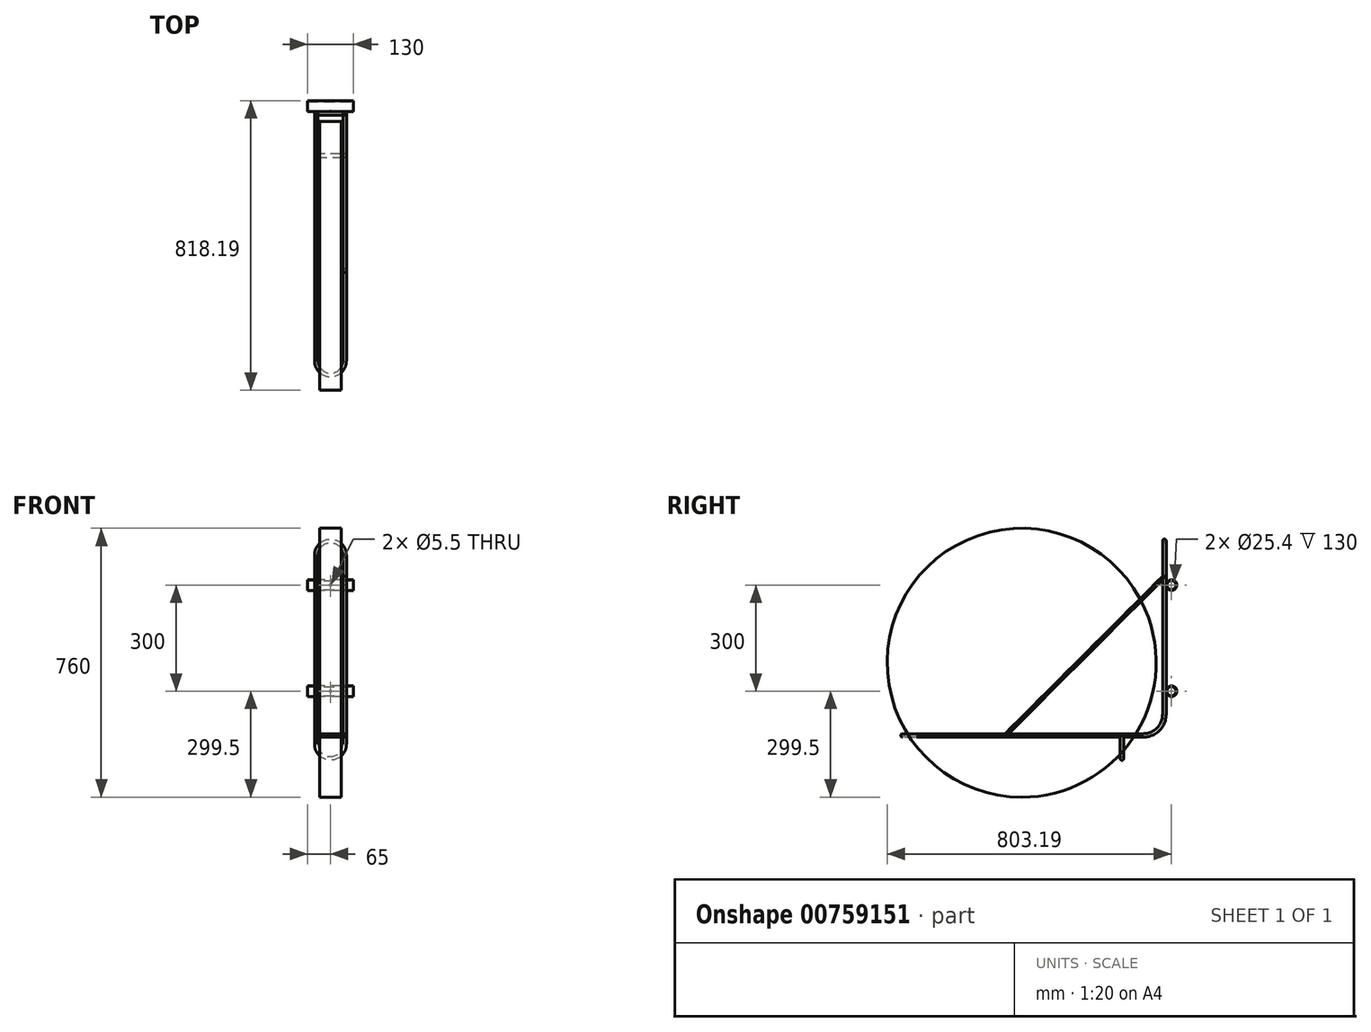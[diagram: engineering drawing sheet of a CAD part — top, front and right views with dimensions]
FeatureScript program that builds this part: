
annotation { "Feature Type Name" : "Feature", "Feature Type Description" : "" }
export const myFeature = defineFeature(function(context is Context, id is Id, definition is map)
    precondition{}
    {
        {
            var Q0;
            Q0=qCreatedBy(makeId("Right.planeOp"),FACE);
            var sketch = newSketch(context, id + "F0", { "sketchPlane" : qUnion([Q0])});
            skLineSegment(sketch, "E0", {"start": v(0, 0) * mm, "end": v(640, 0) * mm});
            skArc(sketch, "E1", {"start": v(640, 0) * mm, "mid": v(682.43, 17.57) * mm, "end": v(700, 60) * mm});
            skLineSegment(sketch, "E2", {"start": v(700, 60) * mm, "end": v(700, 510) * mm});
            skSolve(sketch);
        }
        {
            var Q0;
            Q0=qCreatedBy(makeId("Front.planeOp"),FACE);
            cPlane(context, id + "F1", {"entities" : qUnion([Q0]), "cplaneType" : CPlaneType.OFFSET, "offset" : 700 * mm, "oppositeDirection" : true, "width" : 150 * mm, "height" : 150 * mm});
        }
        {
            var Q0;
            Q0=qCreatedBy(id+"F1.planeOp",FACE);
            var sketch = newSketch(context, id + "F2", { "sketchPlane" : qUnion([Q0])});
            skArc(sketch, "E3", {"start": v(0, 510) * mm, "mid": v(-40, 550) * mm, "end": v(-80, 510) * mm});
            skSolve(sketch);
        }
        {
            var Q0;
            Q0=qCreatedBy(makeId("Front.planeOp"),FACE);
            var sketch = newSketch(context, id + "F3", { "sketchPlane" : qUnion([Q0])});
            skCircle(sketch, "E4", {"center": v(0, 0) * mm, "radius": 5 * mm});
            skSolve(sketch);
        }
        {
            var Q0;
            Q0=qCreatedBy(makeId("Right.planeOp"),FACE);
            cPlane(context, id + "F4", {"entities" : qUnion([Q0]), "cplaneType" : CPlaneType.OFFSET, "offset" : 40 * mm, "oppositeDirection" : true, "width" : 150 * mm, "height" : 150 * mm});
        }
        {
            var Q0;
            Q0=makeQuery(id+"F3.imprint","IMPRINT",FACE,{"disambiguationData":[TD([[makeQuery(id+"F3.imprint","IMPRINT",EDGE,{"derivedFrom":sQuery(id+"F3.wireOp",EDGE,"E4")}),1.0]])]});
            var Q1;
            Q1=sQuery(id+"F0.wireOp",EDGE,"E0");
            var Q2;
            Q2=sQuery(id+"F0.wireOp",EDGE,"E1");
            var Q3;
            Q3=sQuery(id+"F0.wireOp",EDGE,"E2");
            sweep(context, id + "F5", {"profiles" : qUnion([Q0]), "path" : qUnion([Q1, Q2, Q3])});
        }
        {
            var Q0;
            Q0=makeQuery(id+"F5.opSweep","SWEPT_BODY",BODY,{"disambiguationData":[OSD([sQuery(id+"F0.wireOp",EDGE,"E2"),sQuery(id+"F3.wireOp",EDGE,"E4")])]});
            var Q1;
            Q1=qCreatedBy(id+"F4.planeOp",FACE);
            mirror(context, id + "F6", {"entities" : qUnion([Q0]), "mirrorPlane" : qUnion([Q1])});
        }
        {
            var Q0;
            Q0=makeQuery(id+"F5.opSweep","CAP_FACE",FACE,{"disambiguationData":[OSD([sQuery(id+"F0.wireOp",VERTEX,"E2.end"),sQuery(id+"F3.wireOp",EDGE,"E4")])],"isStart":false});
            var Q1;
            Q1=sQuery(id+"F2.wireOp",EDGE,"E3");
            sweep(context, id + "F7", {"operationType" : NewBodyOperationType.ADD, "profiles" : qUnion([Q0]), "path" : qUnion([Q1])});
        }
        {
            var Q0;
            Q0=qCreatedBy(makeId("Top.planeOp"),FACE);
            var sketch = newSketch(context, id + "F8", { "sketchPlane" : qUnion([Q0])});
            skArc(sketch, "E5", {"start": v(-80, 0) * mm, "mid": v(-40, -40) * mm, "end": v(0, 0) * mm});
            skSolve(sketch);
        }
        {
            var Q0;
            Q0=makeQuery(id+"F5.opSweep","CAP_FACE",FACE,{"disambiguationData":[OSD([sQuery(id+"F0.wireOp",VERTEX,"E0.start"),sQuery(id+"F3.wireOp",EDGE,"E4")])],"isStart":true});
            var Q1;
            Q1=sQuery(id+"F8.wireOp",EDGE,"E5");
            sweep(context, id + "F9", {"operationType" : NewBodyOperationType.ADD, "profiles" : qUnion([Q0]), "path" : qUnion([Q1])});
        }
        {
            var Q0;
            Q0=qCreatedBy(makeId("Right.planeOp"),FACE);
            var sketch = newSketch(context, id + "F10", { "sketchPlane" : qUnion([Q0])});
            skLineSegment(sketch, "E6", {"start": v(700, 450) * mm, "end": v(250, 0) * mm});
            skSolve(sketch);
        }
        {
            var Q0;
            Q0=qCreatedBy(id+"F1.planeOp",FACE);
            var sketch = newSketch(context, id + "F11", { "sketchPlane" : qUnion([Q0])});
            skCircle(sketch, "E7", {"center": v(0, 450) * mm, "radius": 5 * mm});
            skSolve(sketch);
        }
        {
            var Q0;
            Q0=makeQuery(id+"F11.imprint","IMPRINT",FACE,{"disambiguationData":[TD([[makeQuery(id+"F11.imprint","IMPRINT",EDGE,{"derivedFrom":sQuery(id+"F11.wireOp",EDGE,"E7")}),1.0]])]});
            var Q1;
            Q1=sQuery(id+"F10.wireOp",EDGE,"E6");
            sweep(context, id + "F12", {"operationType" : NewBodyOperationType.ADD, "profiles" : qUnion([Q0]), "path" : qUnion([Q1])});
        }
        {
            var Q0;
            Q0=qCreatedBy(makeId("Front.planeOp"),FACE);
            cPlane(context, id + "F13", {"entities" : qUnion([Q0]), "cplaneType" : CPlaneType.OFFSET, "offset" : 580 * mm, "oppositeDirection" : true, "width" : 150 * mm, "height" : 150 * mm});
        }
        {
            var Q0;
            Q0=qCreatedBy(id+"F13.planeOp",FACE);
            var sketch = newSketch(context, id + "F14", { "sketchPlane" : qUnion([Q0])});
            skLineSegment(sketch, "E8", {"start": v(0, 0) * mm, "end": v(0, -25) * mm});
            skArc(sketch, "E9", {"start": v(-80, -25) * mm, "mid": v(-40, -65) * mm, "end": v(0, -25) * mm});
            skLineSegment(sketch, "E10", {"start": v(-80, -25) * mm, "end": v(-80, 0) * mm});
            skSolve(sketch);
        }
        {
            var Q0;
            Q0=qCreatedBy(makeId("Top.planeOp"),FACE);
            var sketch = newSketch(context, id + "F15", { "sketchPlane" : qUnion([Q0])});
            skCircle(sketch, "E11", {"center": v(0, 580) * mm, "radius": 5 * mm});
            skSolve(sketch);
        }
        {
            var Q0;
            Q0=makeQuery(id+"F15.imprint","IMPRINT",FACE,{"disambiguationData":[TD([[makeQuery(id+"F15.imprint","IMPRINT",EDGE,{"derivedFrom":sQuery(id+"F15.wireOp",EDGE,"E11")}),1.0]])]});
            var Q1;
            Q1=sQuery(id+"F14.wireOp",EDGE,"E8");
            var Q2;
            Q2=sQuery(id+"F14.wireOp",EDGE,"E9");
            var Q3;
            Q3=sQuery(id+"F14.wireOp",EDGE,"E10");
            sweep(context, id + "F16", {"operationType" : NewBodyOperationType.ADD, "profiles" : qUnion([Q0]), "path" : qUnion([Q1, Q2, Q3])});
        }
        {
            var Q0;
            Q0=qCreatedBy(makeId("Right.planeOp"),FACE);
            var sketch = newSketch(context, id + "F17", { "sketchPlane" : qUnion([Q0])});
            skCircle(sketch, "E12", {"center": v(719.9, 125) * mm, "radius": 15 * mm});
            skCircle(sketch, "E13", {"center": v(719.9, 425) * mm, "radius": 15 * mm});
            skSolve(sketch);
        }
        {
            var Q0;
            Q0=makeQuery(id+"F17.imprint","IMPRINT",FACE,{"disambiguationData":[TD([[makeQuery(id+"F17.imprint","IMPRINT",EDGE,{"derivedFrom":sQuery(id+"F17.wireOp",EDGE,"E13")}),1.0]])]});
            var Q1;
            Q1=makeQuery(id+"F17.imprint","IMPRINT",FACE,{"disambiguationData":[TD([[makeQuery(id+"F17.imprint","IMPRINT",EDGE,{"derivedFrom":sQuery(id+"F17.wireOp",EDGE,"E12")}),1.0]])]});
            var Q2;
            Q2=sQuery(id+"F17.wireOp",EDGE,"E13");
            extrude(context, id + "F18", {"entities" : qUnion([Q0, Q1]), "operationType" : NewBodyOperationType.ADD, "surfaceEntities" : qUnion([Q2]), "depth" : 25 * mm, "offsetDistance" : 25 * mm, "hasSecondDirection" : true, "secondDirectionOppositeDirection" : true, "secondDirectionDepth" : 105 * mm});
        }
        {
            var Q0;
            Q0=makeQuery(id+"F18.opExtrude","CAP_FACE",FACE,{"disambiguationData":[OSD([sQuery(id+"F17.wireOp",EDGE,"E13")])],"isStart":false});
            var sketch = newSketch(context, id + "F19", { "sketchPlane" : qUnion([Q0])});
            skCircle(sketch, "E14", {"center": v(719.9, 425) * mm, "radius": 12.7 * mm});
            skCircle(sketch, "E15", {"center": v(719.9, 125) * mm, "radius": 12.7 * mm});
            skSolve(sketch);
        }
        {
            var Q0;
            Q0=makeQuery(id+"F19.imprint","IMPRINT",FACE,{"disambiguationData":[TD([[makeQuery(id+"F19.imprint","IMPRINT",EDGE,{"derivedFrom":sQuery(id+"F19.wireOp",EDGE,"E14")}),1.0]])]});
            var Q1;
            Q1=makeQuery(id+"F19.imprint","IMPRINT",FACE,{"disambiguationData":[TD([[makeQuery(id+"F19.imprint","IMPRINT",EDGE,{"derivedFrom":sQuery(id+"F19.wireOp",EDGE,"E15")}),1.0]])]});
            extrude(context, id + "F20", {"entities" : qUnion([Q0, Q1]), "operationType" : NewBodyOperationType.REMOVE, "endBound" : BoundingType.THROUGH_ALL, "oppositeDirection" : true, "depth" : 25 * mm, "offsetDistance" : 25 * mm});
        }
        {
            var Q0;
            Q0=qCreatedBy(makeId("Right.planeOp"),FACE);
            cPlane(context, id + "F21", {"entities" : qUnion([Q0]), "cplaneType" : CPlaneType.OFFSET, "offset" : 80 * mm, "oppositeDirection" : true, "width" : 150 * mm, "height" : 150 * mm});
        }
        {
            var Q0;
            Q0=qCreatedBy(id+"F21.planeOp",FACE);
            var sketch = newSketch(context, id + "F22", { "sketchPlane" : qUnion([Q0])});
            skLineSegment(sketch, "E16", {"start": v(250, 0) * mm, "end": v(700, 450) * mm});
            skSolve(sketch);
        }
        {
            var Q0;
            Q0=qCreatedBy(id+"F1.planeOp",FACE);
            var sketch = newSketch(context, id + "F23", { "sketchPlane" : qUnion([Q0])});
            skCircle(sketch, "E17", {"center": v(-80, 450) * mm, "radius": 5 * mm});
            skSolve(sketch);
        }
        {
            var Q0;
            Q0=makeQuery(id+"F23.imprint","IMPRINT",FACE,{"disambiguationData":[TD([[makeQuery(id+"F23.imprint","IMPRINT",EDGE,{"derivedFrom":sQuery(id+"F23.wireOp",EDGE,"E17")}),1.0]])]});
            var Q1;
            Q1=sQuery(id+"F22.wireOp",EDGE,"E16");
            sweep(context, id + "F24", {"operationType" : NewBodyOperationType.ADD, "profiles" : qUnion([Q0]), "path" : qUnion([Q1])});
        }
        {
            var Q0;
            Q0=qCreatedBy(id+"F4.planeOp",FACE);
            var sketch = newSketch(context, id + "F25", { "sketchPlane" : qUnion([Q0])});
            skCircle(sketch, "E18", {"center": v(296.7, 205.5) * mm, "radius": 380 * mm});
            skSolve(sketch);
        }
        {
            var Q0;
            Q0=makeQuery(id+"F25.imprint","IMPRINT",FACE,{"disambiguationData":[TD([[makeQuery(id+"F25.imprint","IMPRINT",EDGE,{"derivedFrom":sQuery(id+"F25.wireOp",EDGE,"E18")}),1.0]])]});
            var Q1;
            Q1=sQuery(id+"F25.wireOp",EDGE,"E18");
            extrude(context, id + "F26", {"entities" : qUnion([Q0]), "surfaceEntities" : qUnion([Q1]), "depth" : 61 * mm, "offsetDistance" : 25 * mm, "symmetric" : true});
        }
        {
            var Q0;
            Q0=qCreatedBy(id+"F1.planeOp",FACE);
            var sketch = newSketch(context, id + "F27", { "sketchPlane" : qUnion([Q0])});
            skPoint(sketch, "E19", {"position": v(-40, 125) * mm});
            skPoint(sketch, "E20", {"position": v(-40, 425) * mm});
            skSolve(sketch);
        }
        {
            var Q0;
            Q0=sQuery(id+"F27.wireOp",VERTEX,"E20");
            var Q1;
            Q1=sQuery(id+"F27.wireOp",VERTEX,"E19");
            var Q2;
            Q2=makeQuery(id+"F5.opSweep","SWEPT_BODY",BODY,{"disambiguationData":[OSD([sQuery(id+"F0.wireOp",EDGE,"E2"),sQuery(id+"F3.wireOp",EDGE,"E4")])]});
            hole(context, id + "F28", {"style" : HoleStyle.SIMPLE, "endStyle" : HoleEndStyle.BLIND, "standardTappedOrClearance" : lookupTablePath({ "standard" : "ISO", "fit" : "Normal", "size" : "M5", "type" : "Clearance" }), "standardBlindInLast" : lookupTablePath({ "fit" : "Standard", "standard" : "ISO", "size" : "M5", "type" : "Clearance" }), "holeDiameter" : 5.5 * mm, "majorDiameter" : 5 * mm, "holeDepth" : 10 * mm, "isTappedThrough" : true, "tappedDepth" : 12 * mm, "tapClearance" : 3, "locations" : qUnion([Q0, Q1]), "scope" : qUnion([Q2]), "startStyle" : HoleStartStyle.PART});
        }
    });
